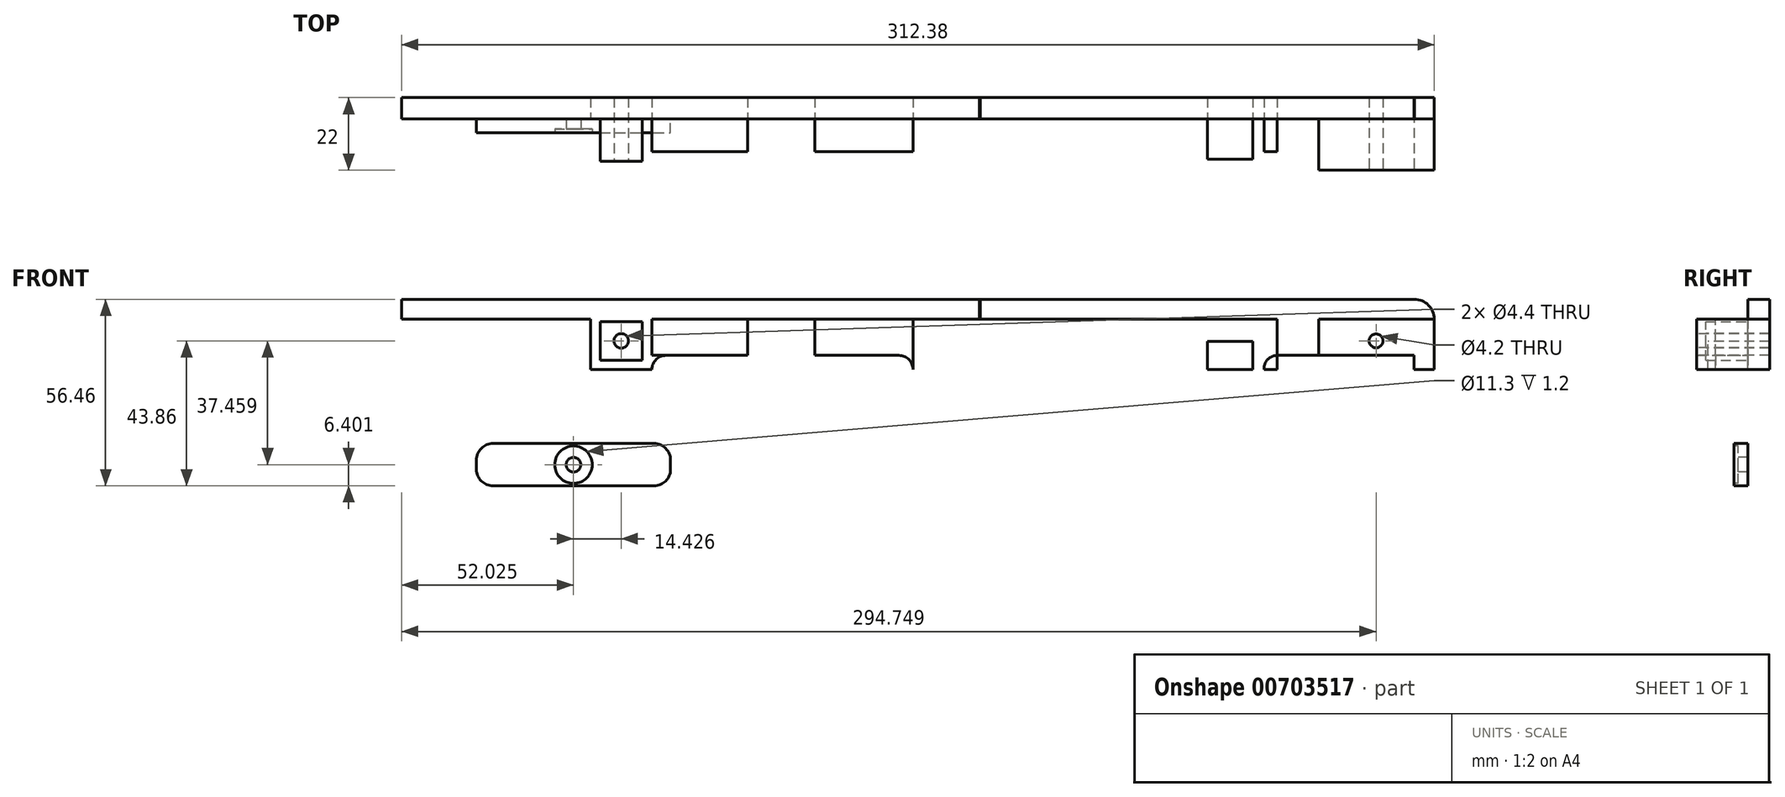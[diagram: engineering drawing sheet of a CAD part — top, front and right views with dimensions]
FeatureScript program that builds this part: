
annotation { "Feature Type Name" : "Feature", "Feature Type Description" : "" }
export const myFeature = defineFeature(function(context is Context, id is Id, definition is map)
    precondition{}
    {
        {
            var Q0;
            Q0=qCreatedBy(makeId("Front.planeOp"),FACE);
            var sketch = newSketch(context, id + "F0", { "sketchPlane" : qUnion([Q0])});
            skLineSegment(sketch, "E0.bottom", {"start": v(-82.5, 21.25) * mm, "end": v(92.5, 21.25) * mm});
            skLineSegment(sketch, "E0.top", {"start": v(-82.5, 0) * mm, "end": v(92.5, 0) * mm});
            skLineSegment(sketch, "E0.left", {"start": v(-82.5, 21.25) * mm, "end": v(-82.5, 0) * mm});
            skLineSegment(sketch, "E0.right", {"start": v(92.5, 21.25) * mm, "end": v(92.5, 0) * mm});
            skLineSegment(sketch, "E1.bottom", {"start": v(-82.5, 0) * mm, "end": v(-25.32, 0) * mm});
            skLineSegment(sketch, "E1.top", {"start": v(-82.5, 15.25) * mm, "end": v(-25.32, 15.25) * mm});
            skLineSegment(sketch, "E1.left", {"start": v(-82.5, 0) * mm, "end": v(-82.5, 15.25) * mm});
            skLineSegment(sketch, "E1.right", {"start": v(-25.32, 0) * mm, "end": v(-25.32, 15.25) * mm});
            skLineSegment(sketch, "E2.right", {"start": v(-9.7, 2.8) * mm, "end": v(-9.7, 14.5) * mm});
            skLineSegment(sketch, "E3", {"start": v(-9.7, 14.5) * mm, "end": v(-22.4, 14.5) * mm});
            skLineSegment(sketch, "E4", {"start": v(-9.7, 2.8) * mm, "end": v(-22.4, 2.8) * mm});
            skLineSegment(sketch, "E5", {"start": v(-6.8, 4.26) * mm, "end": v(72.2, 4.26) * mm});
            skLineSegment(sketch, "E6", {"start": v(72.2, 4.26) * mm, "end": v(72.2, 0.01) * mm});
            skArc(sketch, "E7", {"start": v(-2.54, 4.26) * mm, "mid": v(-5.55, 3.01) * mm, "end": v(-6.8, 0) * mm});
            skArc(sketch, "E8", {"start": v(72.2, 0.01) * mm, "mid": v(70.96, 3.02) * mm, "end": v(67.95, 4.26) * mm});
            skLineSegment(sketch, "E9.bottom", {"start": v(-6.8, 4.26) * mm, "end": v(22.2, 4.26) * mm});
            skLineSegment(sketch, "E9.top", {"start": v(-6.8, 15.25) * mm, "end": v(22.2, 15.25) * mm});
            skLineSegment(sketch, "E9.right", {"start": v(22.2, 4.26) * mm, "end": v(22.2, 15.25) * mm});
            skLineSegment(sketch, "E10.bottom", {"start": v(72.2, 4.26) * mm, "end": v(42.5, 4.26) * mm});
            skLineSegment(sketch, "E10.top", {"start": v(72.2, 15.25) * mm, "end": v(42.5, 15.25) * mm});
            skLineSegment(sketch, "E10.right", {"start": v(42.5, 4.26) * mm, "end": v(42.5, 15.25) * mm});
            skLineSegment(sketch, "E11.bottom", {"start": v(92.5, 0) * mm, "end": v(72.2, 0) * mm});
            skLineSegment(sketch, "E11.top", {"start": v(92.5, 15.25) * mm, "end": v(72.2, 15.25) * mm});
            skLineSegment(sketch, "E11.left", {"start": v(92.5, 0) * mm, "end": v(92.5, 15.25) * mm});
            skLineSegment(sketch, "E11.right", {"start": v(72.2, 0) * mm, "end": v(72.2, 15.25) * mm});
            skLineSegment(sketch, "E12", {"start": v(-6.8, 15.25) * mm, "end": v(-6.8, 4.26) * mm});
            skLineSegment(sketch, "E13", {"start": v(-6.8, 4.26) * mm, "end": v(-6.8, 0) * mm});
            skLineSegment(sketch, "E14", {"start": v(-22.4, 14.5) * mm, "end": v(-22.4, 2.8) * mm});
            skPoint(sketch, "E15", {"position": v(-16.22, 8.92) * mm});
            skLineSegment(sketch, "E16", {"start": v(72.2, 15.25) * mm, "end": v(72.2, 4.26) * mm});
            skLineSegment(sketch, "E17", {"start": v(72.2, 4.26) * mm, "end": v(92.5, 4.26) * mm});
            skLineSegment(sketch, "E18.bottom", {"start": v(42.5, 15.25) * mm, "end": v(92.5, 15.25) * mm});
            skLineSegment(sketch, "E18.top", {"start": v(42.5, 4.26) * mm, "end": v(92.5, 4.26) * mm});
            skLineSegment(sketch, "E18.left", {"start": v(42.5, 15.25) * mm, "end": v(42.5, 4.26) * mm});
            skLineSegment(sketch, "E18.right", {"start": v(92.5, 15.25) * mm, "end": v(92.5, 4.26) * mm});
            skLineSegment(sketch, "E19", {"start": v(72.2, 4.26) * mm, "end": v(72.2, 15.25) * mm});
            skLineSegment(sketch, "E20", {"start": v(-25.32, 15.25) * mm, "end": v(-6.8, 15.25) * mm});
            skLineSegment(sketch, "E21", {"start": v(22.2, 15.25) * mm, "end": v(42.5, 15.25) * mm});
            skSolve(sketch);
        }
        {
            var Q0;
            {var subQ0=sQuery(id+"F0.wireOp",EDGE,"E6");Q0=makeQuery(id+"F0.imprint","IMPRINT",FACE,{"disambiguationData":[TD([[makeQuery(id+"F0.imprint","IMPRINT",EDGE,{"derivedFrom":subQ0}),-1.0]])]});}
            var Q1;
            Q1=makeQuery(id+"F0.imprint","IMPRINT",FACE,{"disambiguationData":[TD([[makeQuery(id+"F0.imprint","IMPRINT",EDGE,{"derivedFrom":sQuery(id+"F0.wireOp",EDGE,"E9.top")}),-1.0]])]});
            var Q2;
            {var subQ0=sQuery(id+"F0.wireOp",EDGE,"E7");Q2=makeQuery(id+"F0.imprint","IMPRINT",FACE,{"disambiguationData":[TD([[makeQuery(id+"F0.imprint","IMPRINT",EDGE,{"derivedFrom":subQ0}),-1.0]])]});}
            var Q3;
            Q3=makeQuery(id+"F0.imprint","IMPRINT",FACE,{"disambiguationData":[TD([[makeQuery(id+"F0.imprint","IMPRINT",EDGE,{"derivedFrom":sQuery(id+"F0.wireOp",EDGE,"E2.right")}),1.0]])]});
            var Q4;
            {var subQ1=sQuery(id+"F0.wireOp",EDGE,"E0.bottom");Q4=makeQuery(id+"F0.imprint","IMPRINT",FACE,{"disambiguationData":[TD([[makeQuery(id+"F0.imprint","IMPRINT",EDGE,{"derivedFrom":subQ1}),-1.0]])]});}
            var Q5;
            Q5=makeQuery(id+"F0.imprint","IMPRINT",FACE,{"disambiguationData":[TD([[makeQuery(id+"F0.imprint","IMPRINT",EDGE,{"derivedFrom":sQuery(id+"F0.wireOp",EDGE,"E10.top")}),1.0]])]});
            var Q6;
            {var subQ0=sQuery(id+"F0.wireOp",EDGE,"E16");Q6=makeQuery(id+"F0.imprint","IMPRINT",FACE,{"disambiguationData":[TD([[makeQuery(id+"F0.imprint","IMPRINT",EDGE,{"derivedFrom":subQ0}),-1.0]])]});}
            var Q7;
            {var subQ5=sQuery(id+"F0.wireOp",EDGE,"E18.right");Q7=makeQuery(id+"F0.imprint","IMPRINT",FACE,{"disambiguationData":[TD([[makeQuery(id+"F0.imprint","IMPRINT",EDGE,{"derivedFrom":subQ5}),-1.0]])]});}
            var Q8;
            {var subQ0=sQuery(id+"F0.wireOp",EDGE,"E19");Q8=makeQuery(id+"F0.imprint","IMPRINT",FACE,{"disambiguationData":[TD([[makeQuery(id+"F0.imprint","IMPRINT",EDGE,{"derivedFrom":subQ0}),1.0]])]});}
            var Q9;
            {var subQ0=sQuery(id+"F0.wireOp",EDGE,"E11.bottom");Q9=makeQuery(id+"F0.imprint","IMPRINT",FACE,{"disambiguationData":[TD([[makeQuery(id+"F0.imprint","IMPRINT",EDGE,{"derivedFrom":subQ0}),-1.0]])]});}
            var Q10;
            Q10=makeQuery(id+"F0.imprint","IMPRINT",FACE,{"disambiguationData":[TD([[makeQuery(id+"F0.imprint","IMPRINT",EDGE,{"derivedFrom":sQuery(id+"F0.wireOp",EDGE,"E1.bottom")}),1.0]])]});
            var Q11;
            {var subQ0=sQuery(id+"F0.wireOp",EDGE,"E1.right");Q11=makeQuery(id+"F0.imprint","IMPRINT",FACE,{"disambiguationData":[TD([[makeQuery(id+"F0.imprint","IMPRINT",EDGE,{"derivedFrom":subQ0}),-1.0]])]});}
            var Q12;
            {var subQ0=sQuery(id+"F0.wireOp",EDGE,"E5");Q12=makeQuery(id+"F0.imprint","IMPRINT",FACE,{"disambiguationData":[TD([[makeQuery(id+"F0.imprint","IMPRINT",EDGE,{"derivedFrom":subQ0}),1.0]])]});}
            var Q13;
            {var subQ0=sQuery(id+"F0.wireOp",EDGE,"E8");Q13=makeQuery(id+"F0.imprint","IMPRINT",FACE,{"disambiguationData":[TD([[makeQuery(id+"F0.imprint","IMPRINT",EDGE,{"derivedFrom":subQ0}),-1.0]])]});}
            extrude(context, id + "F1", {"entities" : qUnion([Q0, Q1, Q2, Q3, Q4, Q5, Q6, Q7, Q8, Q9, Q10, Q11, Q12, Q13]), "depth" : -6.5 * mm, "offsetDistance" : 25 * mm});
        }
        {
            var Q0;
            Q0=makeQuery(id+"F0.imprint","IMPRINT",FACE,{"disambiguationData":[TD([[makeQuery(id+"F0.imprint","IMPRINT",EDGE,{"derivedFrom":sQuery(id+"F0.wireOp",EDGE,"E2.right")}),1.0]])]});
            extrude(context, id + "F2", {"entities" : qUnion([Q0]), "operationType" : NewBodyOperationType.ADD, "depth" : 12.8 * mm, "offsetDistance" : 25 * mm});
        }
        {
            var Q0;
            Q0=makeQuery(id+"F2.opExtrude","CAP_FACE",FACE,{"disambiguationData":[OSD([sQuery(id+"F0.wireOp",EDGE,"E2.right"),sQuery(id+"F0.wireOp",EDGE,"E3"),sQuery(id+"F0.wireOp",EDGE,"E4"),sQuery(id+"F0.wireOp",EDGE,"E14")])],"isStart":false});
            var sketch = newSketch(context, id + "F3", { "sketchPlane" : qUnion([Q0])});
            skPoint(sketch, "E22", {"position": v(-16.06, 8.65) * mm});
            skLineSegment(sketch, "E23", {"start": v(-16.06, 8.65) * mm, "end": v(-16.06, 0) * mm});
            skPoint(sketch, "E23.endSnap0", {"position": v(-16.06, 2.8) * mm});
            skSolve(sketch);
        }
        {
            var Q0;
            Q0=sQuery(id+"F3.wireOp",VERTEX,"E22");
            var Q1;
            Q1=makeQuery(id+"F1.opExtrude","SWEPT_BODY",BODY,{"disambiguationData":[OSD([sQuery(id+"F0.wireOp",EDGE,"E0.bottom"),sQuery(id+"F0.wireOp",EDGE,"E0.top"),sQuery(id+"F0.wireOp",EDGE,"E0.left"),sQuery(id+"F0.wireOp",EDGE,"E1.bottom"),sQuery(id+"F0.wireOp",EDGE,"E1.left"),sQuery(id+"F0.wireOp",EDGE,"E5"),sQuery(id+"F0.wireOp",EDGE,"E7"),sQuery(id+"F0.wireOp",EDGE,"E8"),sQuery(id+"F0.wireOp",EDGE,"pAYxUX9T-Stda-75qX-ZES9-Fa9tSEtQzzwN.right"),sQuery(id+"F0.wireOp",EDGE,"E9.bottom"),sQuery(id+"F0.wireOp",EDGE,"E10.bottom"),sQuery(id+"F0.wireOp",EDGE,"E11.bottom"),sQuery(id+"F0.wireOp",EDGE,"E11.left"),sQuery(id+"F0.wireOp",EDGE,"E11.right")])]});
            hole(context, id + "F4", {"style" : HoleStyle.SIMPLE, "endStyle" : HoleEndStyle.THROUGH, "holeDiameter" : 4.4 * mm, "majorDiameter" : 5 * mm, "isTappedThrough" : true, "tappedDepth" : 12 * mm, "tapClearance" : 3, "locations" : qUnion([Q0]), "scope" : qUnion([Q1])});
        }
        {
            var Q0;
            Q0=qCreatedBy(makeId("Front.planeOp"),FACE);
            var sketch = newSketch(context, id + "F5", { "sketchPlane" : qUnion([Q0])});
            skLineSegment(sketch, "E24.bottom", {"start": v(-59.84, -22.4) * mm, "end": v(-1.14, -22.4) * mm});
            skLineSegment(sketch, "E24.top", {"start": v(-59.84, -35.2) * mm, "end": v(-1.14, -35.2) * mm});
            skLineSegment(sketch, "E24.left", {"start": v(-59.84, -22.4) * mm, "end": v(-59.84, -35.2) * mm});
            skLineSegment(sketch, "E24.right", {"start": v(-1.14, -22.4) * mm, "end": v(-1.14, -35.2) * mm});
            skSolve(sketch);
        }
        {
            var Q0;
            Q0 = qSketchRegion(id + "F5", true);
            extrude(context, id + "F6", {"entities" : qUnion([Q0]), "depth" : 4.2 * mm, "offsetDistance" : 25 * mm});
        }
        {
            var Q0;
            Q0=makeQuery(id+"F6.opExtrude","CAP_FACE",FACE,{"disambiguationData":[OSD([sQuery(id+"F5.wireOp",EDGE,"E24.bottom"),sQuery(id+"F5.wireOp",EDGE,"E24.top"),sQuery(id+"F5.wireOp",EDGE,"E24.left"),sQuery(id+"F5.wireOp",EDGE,"E24.right")])],"isStart":false});
            var sketch = newSketch(context, id + "F7", { "sketchPlane" : qUnion([Q0])});
            skPoint(sketch, "E25", {"position": v(-59.84, -28.8) * mm});
            skPoint(sketch, "E26", {"position": v(-30.49, -35.2) * mm});
            skLineSegment(sketch, "E27", {"start": v(-30.49, -22.4) * mm, "end": v(-30.49, -35.2) * mm});
            skLineSegment(sketch, "E28", {"start": v(-59.84, -28.8) * mm, "end": v(-1.14, -28.8) * mm});
            skPoint(sketch, "E29", {"position": v(-30.49, -28.8) * mm});
            skSolve(sketch);
        }
        {
            var Q0;
            Q0=sQuery(id+"F7.wireOp",VERTEX,"E29");
            var Q1;
            Q1=makeQuery(id+"F6.opExtrude","SWEPT_BODY",BODY,{"disambiguationData":[OSD([sQuery(id+"F5.wireOp",EDGE,"E24.bottom"),sQuery(id+"F5.wireOp",EDGE,"E24.top"),sQuery(id+"F5.wireOp",EDGE,"E24.left"),sQuery(id+"F5.wireOp",EDGE,"E24.right")])]});
            hole(context, id + "F8", {"style" : HoleStyle.C_BORE, "endStyle" : HoleEndStyle.THROUGH, "holeDiameter" : 4.4 * mm, "cBoreDiameter" : 11.3 * mm, "cBoreDepth" : 1.2 * mm, "majorDiameter" : 5 * mm, "isTappedThrough" : true, "tappedDepth" : 12 * mm, "tapClearance" : 3, "locations" : qUnion([Q0]), "scope" : qUnion([Q1])});
        }
        {
            var Q0;
            Q0=makeQuery(id+"F6.opExtrude","SWEPT_EDGE",EDGE,{"disambiguationData":[OSD([sQuery(id+"F5.wireOp",EDGE,"E24.bottom"),sQuery(id+"F5.wireOp",EDGE,"E24.left")])]});
            var Q1;
            Q1=makeQuery(id+"F6.opExtrude","SWEPT_EDGE",EDGE,{"disambiguationData":[OSD([sQuery(id+"F5.wireOp",EDGE,"E24.top"),sQuery(id+"F5.wireOp",EDGE,"E24.left")])]});
            var Q2;
            Q2=makeQuery(id+"F6.opExtrude","SWEPT_EDGE",EDGE,{"disambiguationData":[OSD([sQuery(id+"F5.wireOp",EDGE,"E24.bottom"),sQuery(id+"F5.wireOp",EDGE,"E24.right")])]});
            var Q3;
            Q3=makeQuery(id+"F6.opExtrude","SWEPT_EDGE",EDGE,{"disambiguationData":[OSD([sQuery(id+"F5.wireOp",EDGE,"E24.top"),sQuery(id+"F5.wireOp",EDGE,"E24.right")])]});
            fillet(context, id + "F9", {"entities" : qUnion([Q0, Q1, Q2, Q3]), "radius" : 5 * mm, "tangentPropagation" : true, "allowEdgeOverflow" : false});
        }
        {
            var Q0;
            Q0=makeQuery(id+"F0.imprint","IMPRINT",FACE,{"disambiguationData":[TD([[makeQuery(id+"F0.imprint","IMPRINT",EDGE,{"derivedFrom":sQuery(id+"F0.wireOp",EDGE,"E1.bottom")}),1.0]])]});
            var Q1;
            Q1=makeQuery(id+"F0.imprint","IMPRINT",FACE,{"disambiguationData":[TD([[makeQuery(id+"F0.imprint","IMPRINT",EDGE,{"derivedFrom":sQuery(id+"F0.wireOp",EDGE,"E9.top")}),-1.0]])]});
            var Q2;
            Q2=makeQuery(id+"F0.imprint","IMPRINT",FACE,{"disambiguationData":[TD([[makeQuery(id+"F0.imprint","IMPRINT",EDGE,{"derivedFrom":sQuery(id+"F0.wireOp",EDGE,"E10.top")}),1.0]])]});
            var Q3;
            {var subQ0=sQuery(id+"F0.wireOp",EDGE,"E11.bottom");Q3=makeQuery(id+"F0.imprint","IMPRINT",FACE,{"disambiguationData":[TD([[makeQuery(id+"F0.imprint","IMPRINT",EDGE,{"derivedFrom":subQ0}),-1.0]])]});}
            var Q4;
            {var subQ5=sQuery(id+"F0.wireOp",EDGE,"E18.right");Q4=makeQuery(id+"F0.imprint","IMPRINT",FACE,{"disambiguationData":[TD([[makeQuery(id+"F0.imprint","IMPRINT",EDGE,{"derivedFrom":subQ5}),-1.0]])]});}
            var Q5;
            {var subQ0=sQuery(id+"F0.wireOp",EDGE,"E19");Q5=makeQuery(id+"F0.imprint","IMPRINT",FACE,{"disambiguationData":[TD([[makeQuery(id+"F0.imprint","IMPRINT",EDGE,{"derivedFrom":subQ0}),1.0]])]});}
            var Q6;
            {var subQ0=sQuery(id+"F0.wireOp",EDGE,"E8");var subQ1=sQuery(id+"F0.wireOp",EDGE,"E6");var subQ2=makeQuery(id+"F0.imprint","INTERSECT",VERTEX,{"derivedFrom":[subQ1,subQ0]});Q6=makeQuery(id+"F0.imprint","IMPRINT",FACE,{"disambiguationData":[TD([[makeQuery(id+"F0.imprint","IMPRINT",EDGE,{"disambiguationData":[TD([[subQ2,1.0]])],"derivedFrom":subQ1}),-1.0]])]});}
            var Q7;
            {var subQ0=sQuery(id+"F0.wireOp",EDGE,"E8");Q7=makeQuery(id+"F0.imprint","IMPRINT",FACE,{"disambiguationData":[TD([[makeQuery(id+"F0.imprint","IMPRINT",EDGE,{"derivedFrom":subQ0}),-1.0]])]});}
            extrude(context, id + "F10", {"entities" : qUnion([Q0, Q1, Q2, Q3, Q4, Q5, Q6, Q7]), "operationType" : NewBodyOperationType.ADD, "depth" : 9.8 * mm, "offsetDistance" : 25 * mm});
        }
        {
            var Q0;
            Q0=qCreatedBy(makeId("Front.planeOp"),FACE);
            var sketch = newSketch(context, id + "F11", { "sketchPlane" : qUnion([Q0])});
            skLineSegment(sketch, "E30.MirrorCS", {"start": v(174.95, 0) * mm, "end": v(161.25, 0) * mm});
            skLineSegment(sketch, "E31.MirrorCS", {"start": v(229.87, 0) * mm, "end": v(223.73, 0) * mm});
            skLineSegment(sketch, "E32.MirrorCS", {"start": v(229.87, 21.25) * mm, "end": v(223.73, 21.25) * mm});
            skLineSegment(sketch, "E33.MirrorCS", {"start": v(92.23, 15.25) * mm, "end": v(92.23, 0) * mm});
            skLineSegment(sketch, "E34.MirrorCS", {"start": v(183.39, 15.25) * mm, "end": v(93.73, 15.25) * mm});
            skLineSegment(sketch, "E35.MirrorCS", {"start": v(182.39, 0) * mm, "end": v(92.23, 0) * mm});
            skLineSegment(sketch, "E36.MirrorCS", {"start": v(194.89, 15.25) * mm, "end": v(183.39, 15.25) * mm});
            skLineSegment(sketch, "E37.MirrorCS", {"start": v(223.73, 15.25) * mm, "end": v(205.89, 15.25) * mm});
            skLineSegment(sketch, "E38.MirrorCS", {"start": v(182.39, 15.25) * mm, "end": v(182.39, 4.26) * mm});
            skLineSegment(sketch, "E39.MirrorCS", {"start": v(202.97, 15.25) * mm, "end": v(194.89, 15.25) * mm});
            skLineSegment(sketch, "E40.MirrorCS", {"start": v(202.97, 0) * mm, "end": v(194.89, 0) * mm});
            skLineSegment(sketch, "E41.MirrorCS", {"start": v(223.73, 21.25) * mm, "end": v(223.73, 0) * mm});
            skLineSegment(sketch, "E42.MirrorCS", {"start": v(194.89, 15.25) * mm, "end": v(194.89, 4.26) * mm});
            skLineSegment(sketch, "E43.MirrorCS", {"start": v(223.73, 4.26) * mm, "end": v(194.89, 4.26) * mm});
            skArc(sketch, "E44.MirrorCS", {"start": v(178.35, 0) * mm, "mid": v(179.45, 3) * mm, "end": v(182.39, 4.26) * mm});
            skLineSegment(sketch, "E45.MirrorCS", {"start": v(182.39, 15.25) * mm, "end": v(182.39, 0) * mm});
            skLineSegment(sketch, "E46.MirrorCS", {"start": v(194.89, 4.26) * mm, "end": v(182.39, 4.26) * mm});
            skLineSegment(sketch, "E47.MirrorCS", {"start": v(223.73, 21.25) * mm, "end": v(92.23, 21.25) * mm});
            skLineSegment(sketch, "E48.MirrorCS", {"start": v(161.25, 0) * mm, "end": v(161.25, 8.5) * mm});
            skLineSegment(sketch, "E49.MirrorCS", {"start": v(194.89, 15.25) * mm, "end": v(194.89, 0) * mm});
            skLineSegment(sketch, "E50.MirrorCS", {"start": v(229.87, 21.25) * mm, "end": v(229.87, 0) * mm});
            skLineSegment(sketch, "E51.MirrorCS", {"start": v(223.73, 0) * mm, "end": v(92.23, 0) * mm});
            skLineSegment(sketch, "E52.MirrorCS", {"start": v(202.97, 15.25) * mm, "end": v(202.97, 0) * mm});
            skLineSegment(sketch, "E53.MirrorCS", {"start": v(174.95, 8.5) * mm, "end": v(161.25, 8.5) * mm});
            skLineSegment(sketch, "E54.MirrorCS", {"start": v(92.23, 21.25) * mm, "end": v(92.23, 0) * mm});
            skLineSegment(sketch, "E55.MirrorCS", {"start": v(174.95, 0) * mm, "end": v(174.95, 8.5) * mm});
            skLineSegment(sketch, "E56.MirrorCS", {"start": v(205.89, 15.25) * mm, "end": v(205.89, -0.63) * mm});
            skLineSegment(sketch, "E57.MirrorCS", {"start": v(223.73, 15.25) * mm, "end": v(92.23, 15.25) * mm});
            skLineSegment(sketch, "E58", {"start": v(223.73, 15.25) * mm, "end": v(229.87, 15.25) * mm});
            skArc(sketch, "E59", {"start": v(229.87, 15.25) * mm, "mid": v(228.02, 19.5) * mm, "end": v(223.73, 21.25) * mm});
            skSolve(sketch);
        }
        {
            var Q0;
            {var subQ1=sQuery(id+"F11.wireOp",EDGE,"E44.MirrorCS");Q0=makeQuery(id+"F11.imprint","IMPRINT",FACE,{"disambiguationData":[TD([[makeQuery(id+"F11.imprint","IMPRINT",EDGE,{"derivedFrom":subQ1}),1.0]])]});}
            var Q1;
            {var subQ7=sQuery(id+"F11.wireOp",EDGE,"E41.MirrorCS");Q1=makeQuery(id+"F11.imprint","IMPRINT",FACE,{"disambiguationData":[TD([[makeQuery(id+"F11.imprint","IMPRINT",EDGE,{"derivedFrom":subQ7}),-1.0]])]});}
            var Q2;
            {var subQ0=sQuery(id+"F11.wireOp",EDGE,"E48.MirrorCS");Q2=makeQuery(id+"F11.imprint","IMPRINT",FACE,{"disambiguationData":[TD([[makeQuery(id+"F11.imprint","IMPRINT",EDGE,{"derivedFrom":subQ0}),-1.0]])]});}
            var Q3;
            {var subQ0=sQuery(id+"F11.wireOp",EDGE,"E46.MirrorCS");Q3=makeQuery(id+"F11.imprint","IMPRINT",FACE,{"disambiguationData":[TD([[makeQuery(id+"F11.imprint","IMPRINT",EDGE,{"derivedFrom":subQ0}),-1.0]])]});}
            var Q4;
            {var subQ3=sQuery(id+"F11.wireOp",EDGE,"E52.MirrorCS");var subQ5=sQuery(id+"F11.wireOp",EDGE,"E57.MirrorCS");var subQ7=makeQuery(id+"F11.imprint","INTERSECT",VERTEX,{"derivedFrom":[subQ3,subQ5]});Q4=makeQuery(id+"F11.imprint","IMPRINT",FACE,{"disambiguationData":[TD([[makeQuery(id+"F11.imprint","IMPRINT",EDGE,{"disambiguationData":[TD([[subQ7,-1.0]])],"derivedFrom":subQ3}),-1.0]])]});}
            var Q5;
            {var subQ0=sQuery(id+"F11.wireOp",EDGE,"E41.MirrorCS");var subQ1=sQuery(id+"F11.wireOp",EDGE,"E43.MirrorCS");var subQ2=makeQuery(id+"F11.imprint","INTERSECT",VERTEX,{"derivedFrom":[subQ1,subQ0]});Q5=makeQuery(id+"F11.imprint","IMPRINT",FACE,{"disambiguationData":[TD([[makeQuery(id+"F11.imprint","IMPRINT",EDGE,{"disambiguationData":[TD([[subQ2,-1.0]])],"derivedFrom":subQ1}),-1.0]])]});}
            var Q6;
            {var subQ0=sQuery(id+"F11.wireOp",EDGE,"E56.MirrorCS");var subQ1=sQuery(id+"F11.wireOp",EDGE,"E43.MirrorCS");var subQ2=makeQuery(id+"F11.imprint","INTERSECT",VERTEX,{"derivedFrom":[subQ1,subQ0]});Q6=makeQuery(id+"F11.imprint","IMPRINT",FACE,{"disambiguationData":[TD([[makeQuery(id+"F11.imprint","IMPRINT",EDGE,{"disambiguationData":[TD([[subQ2,-1.0]])],"derivedFrom":subQ1}),-1.0]])]});}
            var Q7;
            {var subQ5=sQuery(id+"F11.wireOp",EDGE,"E31.MirrorCS");Q7=makeQuery(id+"F11.imprint","IMPRINT",FACE,{"disambiguationData":[TD([[makeQuery(id+"F11.imprint","IMPRINT",EDGE,{"derivedFrom":subQ5}),-1.0]])]});}
            var Q8;
            {var subQ5=sQuery(id+"F11.wireOp",EDGE,"E58");Q8=makeQuery(id+"F11.imprint","IMPRINT",FACE,{"disambiguationData":[TD([[makeQuery(id+"F11.imprint","IMPRINT",EDGE,{"derivedFrom":subQ5}),1.0]])]});}
            extrude(context, id + "F12", {"entities" : qUnion([Q0, Q1, Q2, Q3, Q4, Q5, Q6, Q7, Q8]), "depth" : -6.5 * mm, "offsetDistance" : 25 * mm});
        }
        {
            var Q0;
            {var subQ0=sQuery(id+"F11.wireOp",EDGE,"E41.MirrorCS");var subQ1=sQuery(id+"F11.wireOp",EDGE,"E43.MirrorCS");var subQ2=makeQuery(id+"F11.imprint","INTERSECT",VERTEX,{"derivedFrom":[subQ1,subQ0]});Q0=makeQuery(id+"F11.imprint","IMPRINT",FACE,{"disambiguationData":[TD([[makeQuery(id+"F11.imprint","IMPRINT",EDGE,{"disambiguationData":[TD([[subQ2,-1.0]])],"derivedFrom":subQ1}),-1.0]])]});}
            var Q1;
            {var subQ5=sQuery(id+"F11.wireOp",EDGE,"E31.MirrorCS");Q1=makeQuery(id+"F11.imprint","IMPRINT",FACE,{"disambiguationData":[TD([[makeQuery(id+"F11.imprint","IMPRINT",EDGE,{"derivedFrom":subQ5}),-1.0]])]});}
            extrude(context, id + "F13", {"entities" : qUnion([Q0, Q1]), "operationType" : NewBodyOperationType.ADD, "depth" : 15.5 * mm, "offsetDistance" : 25 * mm});
        }
        {
            var Q0;
            {var subQ3=sQuery(id+"F11.wireOp",EDGE,"E52.MirrorCS");var subQ5=sQuery(id+"F11.wireOp",EDGE,"E57.MirrorCS");var subQ7=makeQuery(id+"F11.imprint","INTERSECT",VERTEX,{"derivedFrom":[subQ3,subQ5]});Q0=makeQuery(id+"F11.imprint","IMPRINT",FACE,{"disambiguationData":[TD([[makeQuery(id+"F11.imprint","IMPRINT",EDGE,{"disambiguationData":[TD([[subQ7,-1.0]])],"derivedFrom":subQ3}),-1.0]])]});}
            extrude(context, id + "F14", {"entities" : qUnion([Q0]), "operationType" : NewBodyOperationType.ADD, "depth" : 7.3 * mm, "offsetDistance" : 25 * mm});
        }
        {
            var Q0;
            {var subQ1=sQuery(id+"F11.wireOp",EDGE,"E44.MirrorCS");Q0=makeQuery(id+"F11.imprint","IMPRINT",FACE,{"disambiguationData":[TD([[makeQuery(id+"F11.imprint","IMPRINT",EDGE,{"derivedFrom":subQ1}),1.0]])]});}
            var Q1;
            {var subQ0=sQuery(id+"F11.wireOp",EDGE,"E48.MirrorCS");Q1=makeQuery(id+"F11.imprint","IMPRINT",FACE,{"disambiguationData":[TD([[makeQuery(id+"F11.imprint","IMPRINT",EDGE,{"derivedFrom":subQ0}),-1.0]])]});}
            extrude(context, id + "F15", {"entities" : qUnion([Q0, Q1]), "operationType" : NewBodyOperationType.ADD, "depth" : 9.8 * mm, "offsetDistance" : 25 * mm});
        }
        {
            var Q0;
            {var subQ0=sQuery(id+"F11.wireOp",EDGE,"E48.MirrorCS");Q0=makeQuery(id+"F11.imprint","IMPRINT",FACE,{"disambiguationData":[TD([[makeQuery(id+"F11.imprint","IMPRINT",EDGE,{"derivedFrom":subQ0}),-1.0]])]});}
            extrude(context, id + "F16", {"entities" : qUnion([Q0]), "operationType" : NewBodyOperationType.ADD, "depth" : 12.1 * mm, "offsetDistance" : 25 * mm});
        }
        {
            var Q0;
            Q0=makeQuery(id+"F15.opExtrude","CAP_FACE",FACE,{"disambiguationData":[OSD([sQuery(id+"F11.wireOp",EDGE,"E44.MirrorCS"),sQuery(id+"F11.wireOp",EDGE,"E45.MirrorCS"),sQuery(id+"F11.wireOp",EDGE,"E51.MirrorCS"),sQuery(id+"F11.wireOp",EDGE,"E54.MirrorCS"),sQuery(id+"F11.wireOp",EDGE,"E57.MirrorCS")])],"isStart":false});
            var sketch = newSketch(context, id + "F17", { "sketchPlane" : qUnion([Q0])});
            skPoint(sketch, "E60", {"position": v(126.7, 8.65) * mm});
            skLineSegment(sketch, "E61", {"start": v(126.7, 8.65) * mm, "end": v(126.7, 0) * mm});
            skSolve(sketch);
        }
        {
            var Q0;
            Q0=sQuery(id+"F17.wireOp",VERTEX,"E60");
            var Q1;
            Q1=makeQuery(id+"F12.opExtrude","SWEPT_BODY",BODY,{"disambiguationData":[OSD([sQuery(id+"F11.wireOp",EDGE,"E31.MirrorCS"),sQuery(id+"F11.wireOp",EDGE,"E32.MirrorCS"),sQuery(id+"F11.wireOp",EDGE,"E41.MirrorCS"),sQuery(id+"F11.wireOp",EDGE,"E43.MirrorCS"),sQuery(id+"F11.wireOp",EDGE,"E44.MirrorCS"),sQuery(id+"F11.wireOp",EDGE,"E41.MirrorCS"),sQuery(id+"F11.wireOp",EDGE,"E46.MirrorCS"),sQuery(id+"F11.wireOp",EDGE,"E47.MirrorCS"),sQuery(id+"F11.wireOp",EDGE,"E50.MirrorCS"),sQuery(id+"F11.wireOp",EDGE,"E51.MirrorCS"),sQuery(id+"F11.wireOp",EDGE,"E54.MirrorCS"),sQuery(id+"F11.wireOp",EDGE,"E59")])]});
            hole(context, id + "F18", {"style" : HoleStyle.SIMPLE, "endStyle" : HoleEndStyle.THROUGH, "holeDiameter" : 3.8 * mm, "majorDiameter" : 5 * mm, "isTappedThrough" : true, "tappedDepth" : 12 * mm, "tapClearance" : 3, "locations" : qUnion([Q0]), "scope" : qUnion([Q1])});
        }
        {
            var Q0;
            Q0=makeQuery(id+"F13.opExtrude","CAP_FACE",FACE,{"disambiguationData":[OSD([sQuery(id+"F11.wireOp",EDGE,"E31.MirrorCS"),sQuery(id+"F11.wireOp",EDGE,"E43.MirrorCS"),sQuery(id+"F11.wireOp",EDGE,"E41.MirrorCS"),sQuery(id+"F11.wireOp",EDGE,"E50.MirrorCS"),sQuery(id+"F11.wireOp",EDGE,"E56.MirrorCS"),sQuery(id+"F11.wireOp",EDGE,"E57.MirrorCS"),sQuery(id+"F11.wireOp",EDGE,"E58")])],"isStart":false});
            var sketch = newSketch(context, id + "F19", { "sketchPlane" : qUnion([Q0])});
            skPoint(sketch, "E62", {"position": v(212.24, 8.65) * mm});
            skLineSegment(sketch, "E63", {"start": v(212.24, 8.65) * mm, "end": v(212.24, 0) * mm});
            skSolve(sketch);
        }
        {
            var Q0;
            Q0=sQuery(id+"F19.wireOp",VERTEX,"E62");
            var Q1;
            Q1=makeQuery(id+"F12.opExtrude","SWEPT_BODY",BODY,{"disambiguationData":[OSD([sQuery(id+"F11.wireOp",EDGE,"E31.MirrorCS"),sQuery(id+"F11.wireOp",EDGE,"E32.MirrorCS"),sQuery(id+"F11.wireOp",EDGE,"E41.MirrorCS"),sQuery(id+"F11.wireOp",EDGE,"E43.MirrorCS"),sQuery(id+"F11.wireOp",EDGE,"E44.MirrorCS"),sQuery(id+"F11.wireOp",EDGE,"E41.MirrorCS"),sQuery(id+"F11.wireOp",EDGE,"E46.MirrorCS"),sQuery(id+"F11.wireOp",EDGE,"E47.MirrorCS"),sQuery(id+"F11.wireOp",EDGE,"E50.MirrorCS"),sQuery(id+"F11.wireOp",EDGE,"E51.MirrorCS"),sQuery(id+"F11.wireOp",EDGE,"E54.MirrorCS"),sQuery(id+"F11.wireOp",EDGE,"E59")])]});
            hole(context, id + "F20", {"style" : HoleStyle.SIMPLE, "endStyle" : HoleEndStyle.THROUGH, "holeDiameter" : 4.2 * mm, "majorDiameter" : 5 * mm, "isTappedThrough" : true, "tappedDepth" : 12 * mm, "tapClearance" : 3, "locations" : qUnion([Q0]), "scope" : qUnion([Q1])});
        }
    });
